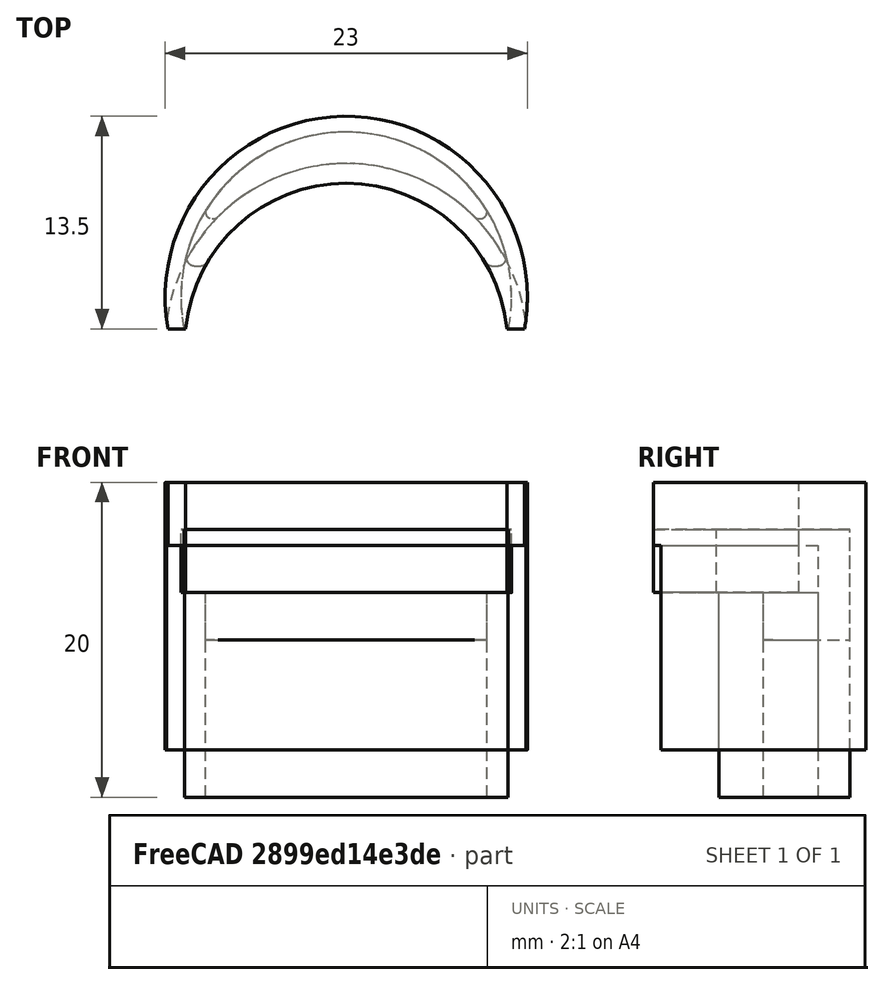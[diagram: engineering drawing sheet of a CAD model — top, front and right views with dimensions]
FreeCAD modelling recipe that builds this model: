
FCSTD DOCUMENT  (FreeCAD 0.18R4 (GitTag))
Label: ajuste_ducha
License: CreativeCommons Attribution-ShareAlike
LicenseURL: http://creativecommons.org/licenses/by-sa/4.0/
objects: Part::Cut×6, Part::Cylinder×4, Part::Box×4, Part::Feature×3, Part::Fillet×3, Part::MultiFuse×1
note: 21 computed .brp shape members not serialized (recipe doc carries the construction recipe); baked Part::Feature solids carry a one-line shape summary decoded from their .brp

FEATURE [Part::Cylinder] Cylinder  label="ajustar_este"
  Angle = 360
  AttacherType = Attacher::AttachEngine3D
  Height = 20
  Radius = 10.5
FEATURE [Part::Cylinder] Cylinder001
  Angle = 360
  AttacherType = Attacher::AttachEngine3D
  Height = 20
  Radius = 20
FEATURE [Part::Cut] Cut
  Base = -> Cylinder001
  Tool = -> Cylinder
FEATURE [Part::Cylinder] Cylinder002
  Angle = 360
  AttacherType = Attacher::AttachEngine3D
  Height = 13
  Placement = pos=(0,-3,0) rot=(0,0,1;0rad)
  Radius = 11.5
FEATURE [Part::Cylinder] Cylinder003
  Angle = 360
  AttacherType = Attacher::AttachEngine3D
  Height = 17
  Placement = pos=(0,-3,0) rot=(0,0,1;0rad)
  Radius = 10.25
FEATURE [Part::MultiFuse] Fusion
  Shapes = -> [Cylinder002,Cylinder003]
FEATURE [Part::Box] Box  label="Cube"
  AttacherType = Attacher::AttachEngine3D
  Height = 17
  Length = 26
  Placement = pos=(-13,-2,0) rot=(0,0,1;0rad)
  Width = 15
FEATURE [Part::Cut] Cut001
  Base = -> Box
  Tool = -> Fusion
FEATURE [Part::Cut] Cut002  label="parte_chica1"
  Base = -> Cut001
  Tool = -> Cut
FEATURE [Part::Feature] Cut002001  label="parte_1250"
  Placement = pos=(0,0,3) rot=(0,0,1;0rad)
  shape: bbox 23 x 13.5 x 17 mm, 8 faces (baked)
FEATURE [Part::Feature] Cut002002  label="parte_1050"
  shape: bbox 21 x 12.5 x 17 mm, 8 faces (baked)
FEATURE [Part::Box] Box001  label="Cube001"
  AttacherType = Attacher::AttachEngine3D
  Height = 17
  Length = 30
  Placement = pos=(-15,-8,0) rot=(0,0,1;0rad)
  Width = 10
FEATURE [Part::Box] Box002  label="Cube002"
  AttacherType = Attacher::AttachEngine3D
  Height = 13
  Length = 30
  Placement = pos=(-15,-5,0) rot=(0,0,1;0rad)
  Width = 10
FEATURE [Part::Cut] Cut002003
  Base = -> Cut002
  Tool = -> Box001
FEATURE [Part::Cut] Cut002004
  Base = -> Cut002003
  Tool = -> Box002
FEATURE [Part::Fillet] Fillet
  Base = -> Cut002004
  Edges = 4 edges r=0.4: [Edge5,Edge7,Edge21,Edge25]
FEATURE [Part::Fillet] Fillet001
  Base = -> Fillet
  Edges = 2 edges r=0.55: [Edge10,Edge37]
FEATURE [Part::Fillet] Fillet002
  Base = -> Fillet001
  Edges = 2 edges r=0.55: [Edge6,Edge27]
FEATURE [Part::Feature] Fillet002001  label="Fillet003"
  shape: bbox 20.34 x 8.5 x 17 mm, 18 faces (baked)
FEATURE [Part::Box] Box003  label="Cube003"
  AttacherType = Attacher::AttachEngine3D
  Height = 10
  Length = 30
  Placement = pos=(-15,-10,0) rot=(0,0,1;0rad)
  Width = 30
FEATURE [Part::Cut] Cut002005
  Base = -> Fillet002001
  Tool = -> Box003
